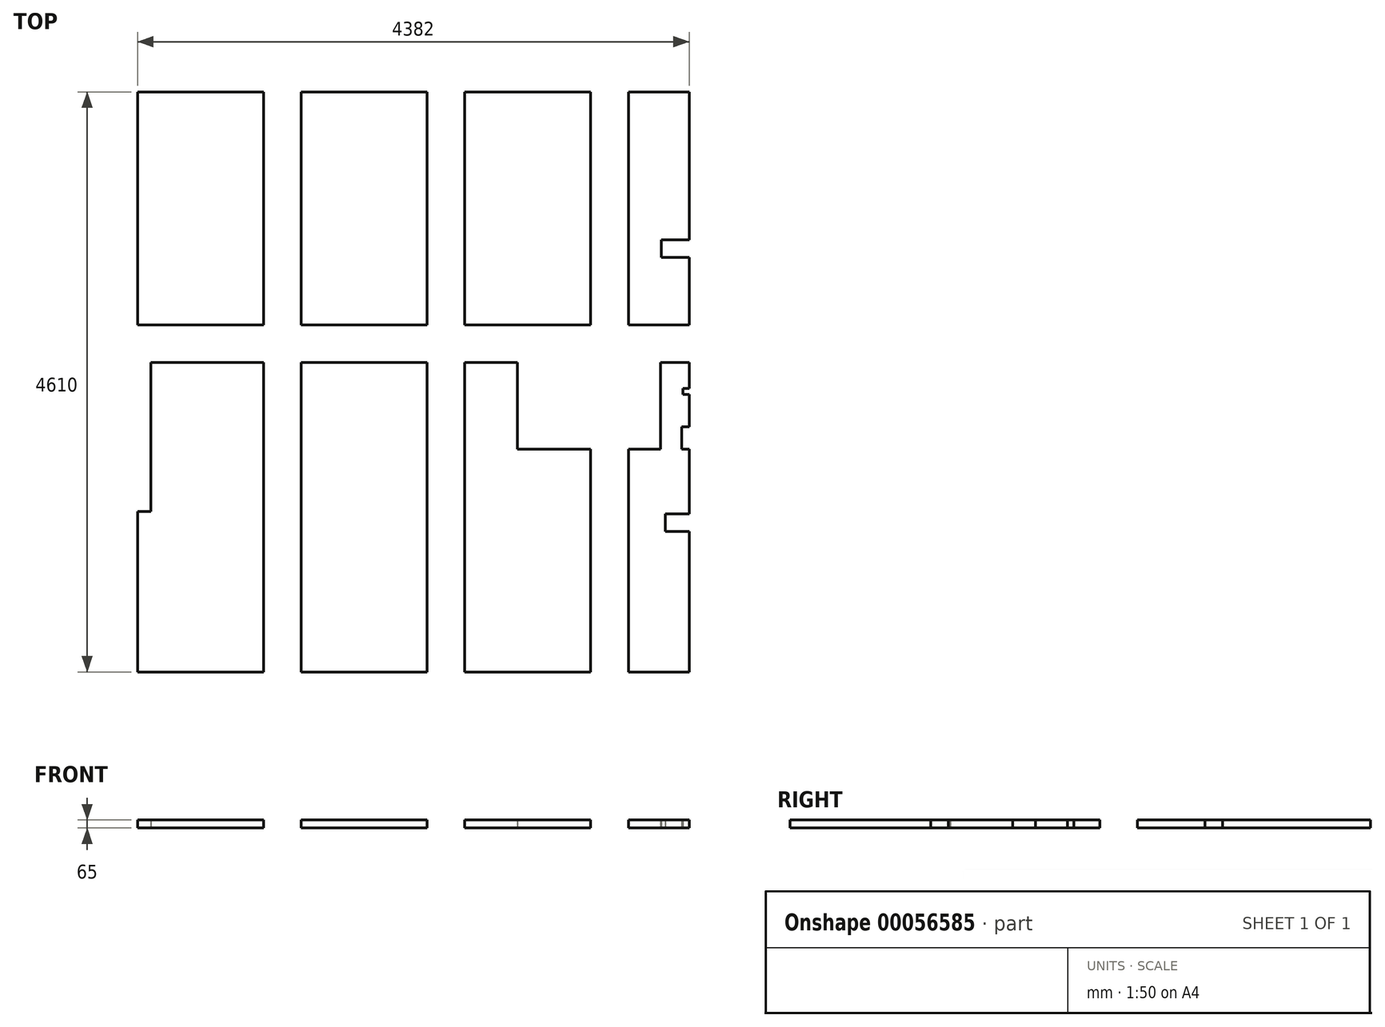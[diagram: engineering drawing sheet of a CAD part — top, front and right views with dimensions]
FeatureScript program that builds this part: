
annotation { "Feature Type Name" : "Feature", "Feature Type Description" : "" }
export const myFeature = defineFeature(function(context is Context, id is Id, definition is map)
    precondition{}
    {
        {
            var Q0;
            Q0=qCreatedBy(makeId("Top.planeOp"),FACE);
            var sketch = newSketch(context, id + "F0", { "sketchPlane" : qUnion([Q0])});
            skLineSegment(sketch, "E0.bottom", {"start": v(-538.83, 941.87) * mm, "end": v(461.17, 941.87) * mm});
            skLineSegment(sketch, "E0.top", {"start": v(-538.83, -908.13) * mm, "end": v(461.17, -908.13) * mm});
            skLineSegment(sketch, "E0.left", {"start": v(-538.83, 941.87) * mm, "end": v(-538.83, -908.13) * mm});
            skLineSegment(sketch, "E0.right", {"start": v(461.17, 941.87) * mm, "end": v(461.17, -908.13) * mm});
            skLineSegment(sketch, "E1.top", {"start": v(761.17, -908.13) * mm, "end": v(1761.17, -908.13) * mm});
            skLineSegment(sketch, "E1.left", {"start": v(761.17, 941.87) * mm, "end": v(761.17, -908.13) * mm});
            skLineSegment(sketch, "E1.right", {"start": v(1761.17, 941.87) * mm, "end": v(1761.17, -908.13) * mm});
            skLineSegment(sketch, "E1.bottom", {"start": v(761.17, 941.87) * mm, "end": v(1761.17, 941.87) * mm});
            skLineSegment(sketch, "E2.top", {"start": v(2061.17, -908.13) * mm, "end": v(3061.17, -908.13) * mm});
            skLineSegment(sketch, "E2.left", {"start": v(2061.17, 941.87) * mm, "end": v(2061.17, -908.13) * mm});
            skLineSegment(sketch, "E2.right", {"start": v(3061.17, 941.87) * mm, "end": v(3061.17, -908.13) * mm});
            skLineSegment(sketch, "E2.bottom", {"start": v(2061.17, 941.87) * mm, "end": v(3061.17, 941.87) * mm});
            skLineSegment(sketch, "E3.top", {"start": v(3361.17, -908.13) * mm, "end": v(3843.17, -908.13) * mm});
            skLineSegment(sketch, "E3.left", {"start": v(3361.17, 941.87) * mm, "end": v(3361.17, -908.13) * mm});
            skLineSegment(sketch, "E3.right", {"start": v(3843.17, 941.87) * mm, "end": v(3843.17, -232.13) * mm});
            skLineSegment(sketch, "E3.bottom", {"start": v(3361.17, 941.87) * mm, "end": v(3843.17, 941.87) * mm});
            skLineSegment(sketch, "E4.bottom", {"start": v(3843.17, -232.13) * mm, "end": v(3623.17, -232.13) * mm});
            skLineSegment(sketch, "E4.top", {"start": v(3843.17, -372.13) * mm, "end": v(3623.17, -372.13) * mm});
            skLineSegment(sketch, "E4.right", {"start": v(3623.17, -232.13) * mm, "end": v(3623.17, -372.13) * mm});
            skLineSegment(sketch, "E5.trimOffspring", {"start": v(3843.17, -372.13) * mm, "end": v(3843.17, -908.13) * mm});
            skLineSegment(sketch, "E6.bottom", {"start": v(-433.83, -1208.13) * mm, "end": v(461.17, -1208.13) * mm});
            skLineSegment(sketch, "E6.top", {"start": v(-538.83, -3668.13) * mm, "end": v(461.17, -3668.13) * mm});
            skLineSegment(sketch, "E6.left", {"start": v(-538.83, -2393.13) * mm, "end": v(-538.83, -3668.13) * mm});
            skLineSegment(sketch, "E6.right", {"start": v(461.17, -1208.13) * mm, "end": v(461.17, -3668.13) * mm});
            skLineSegment(sketch, "E7.top", {"start": v(-538.83, -2393.13) * mm, "end": v(-433.83, -2393.13) * mm});
            skLineSegment(sketch, "E7.right", {"start": v(-433.83, -1208.13) * mm, "end": v(-433.83, -2393.13) * mm});
            skLineSegment(sketch, "E8.bottom", {"start": v(761.17, -1208.13) * mm, "end": v(1761.17, -1208.13) * mm});
            skLineSegment(sketch, "E8.top", {"start": v(761.17, -3668.13) * mm, "end": v(1761.17, -3668.13) * mm});
            skLineSegment(sketch, "E8.left", {"start": v(761.17, -1208.13) * mm, "end": v(761.17, -3668.13) * mm});
            skLineSegment(sketch, "E8.right", {"start": v(1761.17, -1208.13) * mm, "end": v(1761.17, -3668.13) * mm});
            skLineSegment(sketch, "E9.bottom", {"start": v(2061.17, -1208.13) * mm, "end": v(2479.17, -1208.13) * mm});
            skLineSegment(sketch, "E9.top", {"start": v(2061.17, -3668.13) * mm, "end": v(3061.17, -3668.13) * mm});
            skLineSegment(sketch, "E9.left", {"start": v(2061.17, -1208.13) * mm, "end": v(2061.17, -3668.13) * mm});
            skLineSegment(sketch, "E9.right", {"start": v(3061.17, -1898.13) * mm, "end": v(3061.17, -3668.13) * mm});
            skLineSegment(sketch, "E10.top", {"start": v(3061.17, -1898.13) * mm, "end": v(2479.17, -1898.13) * mm});
            skLineSegment(sketch, "E10.right", {"start": v(2479.17, -1208.13) * mm, "end": v(2479.17, -1898.13) * mm});
            skLineSegment(sketch, "E11.bottom", {"start": v(3615.17, -1208.13) * mm, "end": v(3843.17, -1208.13) * mm});
            skLineSegment(sketch, "E11.top", {"start": v(3361.17, -3668.13) * mm, "end": v(3843.17, -3668.13) * mm});
            skLineSegment(sketch, "E11.left", {"start": v(3361.17, -1898.13) * mm, "end": v(3361.17, -3668.13) * mm});
            skLineSegment(sketch, "E11.right", {"start": v(3843.17, -1208.13) * mm, "end": v(3843.17, -1413.13) * mm});
            skLineSegment(sketch, "E12.top", {"start": v(3361.17, -1898.13) * mm, "end": v(3615.17, -1898.13) * mm});
            skLineSegment(sketch, "E12.right", {"start": v(3615.17, -1208.13) * mm, "end": v(3615.17, -1898.13) * mm});
            skLineSegment(sketch, "E13.bottom", {"start": v(3843.17, -1413.13) * mm, "end": v(3793.17, -1413.13) * mm});
            skLineSegment(sketch, "E13.top", {"start": v(3843.17, -1463.13) * mm, "end": v(3793.17, -1463.13) * mm});
            skLineSegment(sketch, "E13.right", {"start": v(3793.17, -1413.13) * mm, "end": v(3793.17, -1463.13) * mm});
            skLineSegment(sketch, "E14.bottom", {"start": v(3843.17, -1718.13) * mm, "end": v(3783.17, -1718.13) * mm});
            skLineSegment(sketch, "E14.top", {"start": v(3843.17, -1898.13) * mm, "end": v(3783.17, -1898.13) * mm});
            skLineSegment(sketch, "E14.right", {"start": v(3783.17, -1718.13) * mm, "end": v(3783.17, -1898.13) * mm});
            skLineSegment(sketch, "E15.bottom", {"start": v(3843.17, -2410.13) * mm, "end": v(3653.17, -2410.13) * mm});
            skLineSegment(sketch, "E15.top", {"start": v(3843.17, -2550.13) * mm, "end": v(3653.17, -2550.13) * mm});
            skLineSegment(sketch, "E15.right", {"start": v(3653.17, -2410.13) * mm, "end": v(3653.17, -2550.13) * mm});
            skLineSegment(sketch, "E16.trimOffspring", {"start": v(3843.17, -1463.13) * mm, "end": v(3843.17, -1718.13) * mm});
            skLineSegment(sketch, "E17.trimOffspring", {"start": v(3843.17, -1898.13) * mm, "end": v(3843.17, -2410.13) * mm});
            skLineSegment(sketch, "E18.trimOffspring", {"start": v(3843.17, -2550.13) * mm, "end": v(3843.17, -3668.13) * mm});
            skSolve(sketch);
        }
        {
            var Q0;
            Q0 = qSketchRegion(id + "F0", true);
            extrude(context, id + "F1", {"entities" : qUnion([Q0]), "depth" : 65 * mm});
        }
    });
